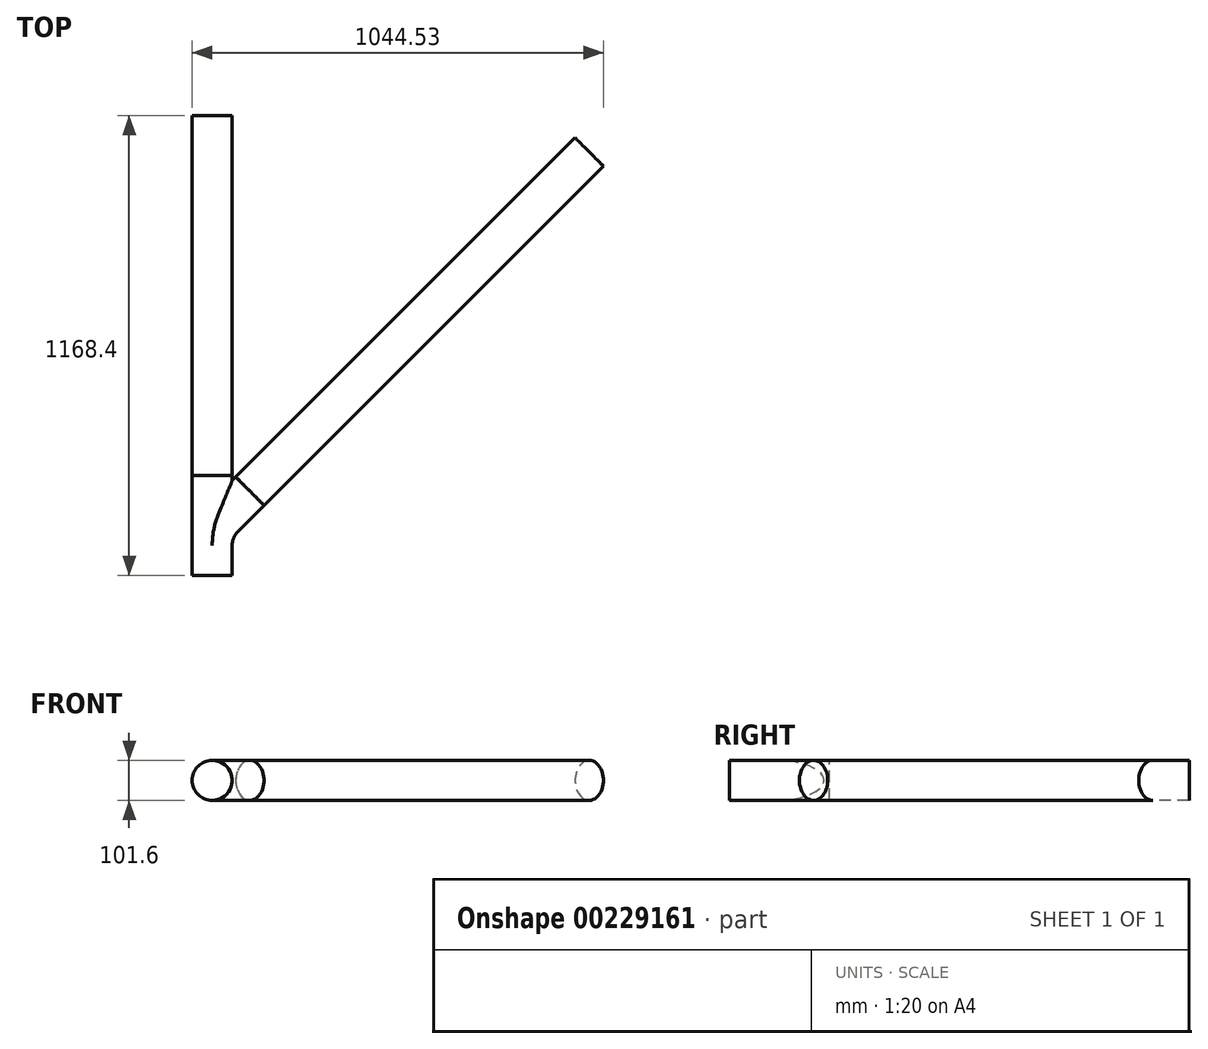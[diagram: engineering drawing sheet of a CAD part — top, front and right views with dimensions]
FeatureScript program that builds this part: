
annotation { "Feature Type Name" : "Feature", "Feature Type Description" : "" }
export const myFeature = defineFeature(function(context is Context, id is Id, definition is map)
    precondition{}
    {
        {
            var Q0;
            Q0=qCreatedBy(makeId("Top.planeOp"),FACE);
            var sketch = newSketch(context, id + "F0", { "sketchPlane" : qUnion([Q0])});
            skLineSegment(sketch, "E0", {"start": v(95.7, 213.99) * mm, "end": v(29.76, 148.04) * mm});
            skPoint(sketch, "E1.visualSharp", {"position": v(0, 0) * mm});
            skArc(sketch, "E1.filletArc", {"start": v(29.76, 148.04) * mm, "mid": v(7.73, 115.08) * mm, "end": v(0, 76.2) * mm});
            skLineSegment(sketch, "E2", {"start": v(0, 76.2) * mm, "end": v(0, 0) * mm});
            skLineSegment(sketch, "E3", {"start": v(0, 76.2) * mm, "end": v(0, 254) * mm});
            skLineSegment(sketch, "E4", {"start": v(29.76, 148.04) * mm, "end": v(0, 118.28) * mm});
            skLineSegment(sketch, "E5", {"start": v(0, 118.28) * mm, "end": v(95.7, 118.28) * mm, "construction": true});
            skLineSegment(sketch, "E6", {"start": v(95.7, 118.28) * mm, "end": v(95.7, 213.99) * mm, "construction": true});
            skLineSegment(sketch, "E7", {"start": v(0, 76.2) * mm, "end": v(116.74, 192.94) * mm});
            skLineSegment(sketch, "E8", {"start": v(116.74, 192.94) * mm, "end": v(95.7, 213.99) * mm});
            skLineSegment(sketch, "E9", {"start": v(101.6, 76.2) * mm, "end": v(0, 76.2) * mm});
            skSolve(sketch);
        }
        {
            var Q0;
            Q0=qCreatedBy(makeId("Front.planeOp"),FACE);
            var sketch = newSketch(context, id + "F1", { "sketchPlane" : qUnion([Q0])});
            skCircle(sketch, "E10", {"center": v(0, 0) * mm, "radius": 50.8 * mm});
            skSolve(sketch);
        }
        {
            var Q0;
            Q0=makeQuery(id+"F1.imprint","IMPRINT",FACE,{"disambiguationData":[TD([[makeQuery(id+"F1.imprint","IMPRINT",EDGE,{"derivedFrom":sQuery(id+"F1.wireOp",EDGE,"E10")}),1.0]])]});
            var Q1;
            Q1=sQuery(id+"F0.wireOp",EDGE,"E2");
            var Q2;
            Q2=sQuery(id+"F0.wireOp",EDGE,"E1.filletArc");
            var Q3;
            Q3=sQuery(id+"F0.wireOp",EDGE,"E0");
            sweep(context, id + "F2", {"profiles" : qUnion([Q0]), "path" : qUnion([Q1, Q2, Q3])});
        }
        {
            var Q0;
            Q0=makeQuery(id+"F1.imprint","IMPRINT",FACE,{"disambiguationData":[TD([[makeQuery(id+"F1.imprint","IMPRINT",EDGE,{"derivedFrom":sQuery(id+"F1.wireOp",EDGE,"E10")}),1.0]])]});
            var Q1;
            Q1=sQuery(id+"F0.wireOp",EDGE,"E2");
            var Q2;
            Q2=sQuery(id+"F0.wireOp",EDGE,"E3");
            sweep(context, id + "F3", {"operationType" : NewBodyOperationType.ADD, "profiles" : qUnion([Q0]), "path" : qUnion([Q1, Q2])});
        }
        {
            var Q0;
            Q0=makeQuery(id+"F2.opSweep","SWEPT_BODY",BODY,{"disambiguationData":[OSD([sQuery(id+"F0.wireOp",EDGE,"E0"),sQuery(id+"F1.wireOp",EDGE,"E10")])]});
            transform(context, id + "F4", {"entities" : qUnion([Q0]), "transformType" : TransformType.TRANSLATION_3D, "dx" : 0 * mm, "dy" : 0 * mm, "dz" : 0 * mm, "makeCopy" : true});
        }
        {
            var Q0;
            Q0=makeQuery(id+"F2.opSweep","CAP_FACE",FACE,{"disambiguationData":[OSD([sQuery(id+"F0.wireOp",VERTEX,"E0.start"),sQuery(id+"F1.wireOp",EDGE,"E10")])],"isStart":false});
            extrude(context, id + "F5", {"entities" : qUnion([Q0]), "depth" : 1219.2 * mm});
        }
        {
            var Q0;
            Q0=makeQuery(id+"F3.opSweep","CAP_FACE",FACE,{"disambiguationData":[OSD([sQuery(id+"F0.wireOp",VERTEX,"E3.end"),sQuery(id+"F1.wireOp",EDGE,"E10")])],"isStart":false});
            extrude(context, id + "F6", {"entities" : qUnion([Q0]), "depth" : 914.4 * mm});
        }
    });
